# Revit family: mcr FID-120-НЗ-C1-AxB ЗМ
name_source: partatom
category: Арматура воздуховодов
revit_build: Autodesk Revit 2016 (Build: 20150714_1515(x64)
units: mm (PartAtom-declared; Revit-internal decimal feet)

## family parameters
Общий = Нет
Основа = Грань
При загрузке вырезать с полостями = Нет
Размер круглого соединителя = Использовать диаметр
Тип детали = Вставляется

## types (1)
- mcr FID-120-НЗ-C1-AxB ЗМ
    ADSK_Масса = 0
    ADSK_Предел огнестойкости = EI120
    BE230 = Нет
    BE24 = Нет
    BF230 = Нет
    BF24 = Нет
    BFL230 = Нет
    BFL24 = Нет
    BFN230 = Нет
    BFN24 = Нет
    BLE230 = Нет
    BLE24 = Нет
    MM230 = Нет
    MM24 = Нет
    P = 1.2000 кг/куб. м
    t_заслонки = 20 мм
    t_перегородки = 20 мм
    Бренд = Mercor Proof
    Материал клапана = <По категории>
    Оснащение привода саморегулирующимся нагревательным кабелем = Нет
    Отметка по умолчанию = 0 мм
    Термодатчик = Нет

## geometry (parser evidence)
native form markers: Blend x2
no freeform markers — native parametric forms only
